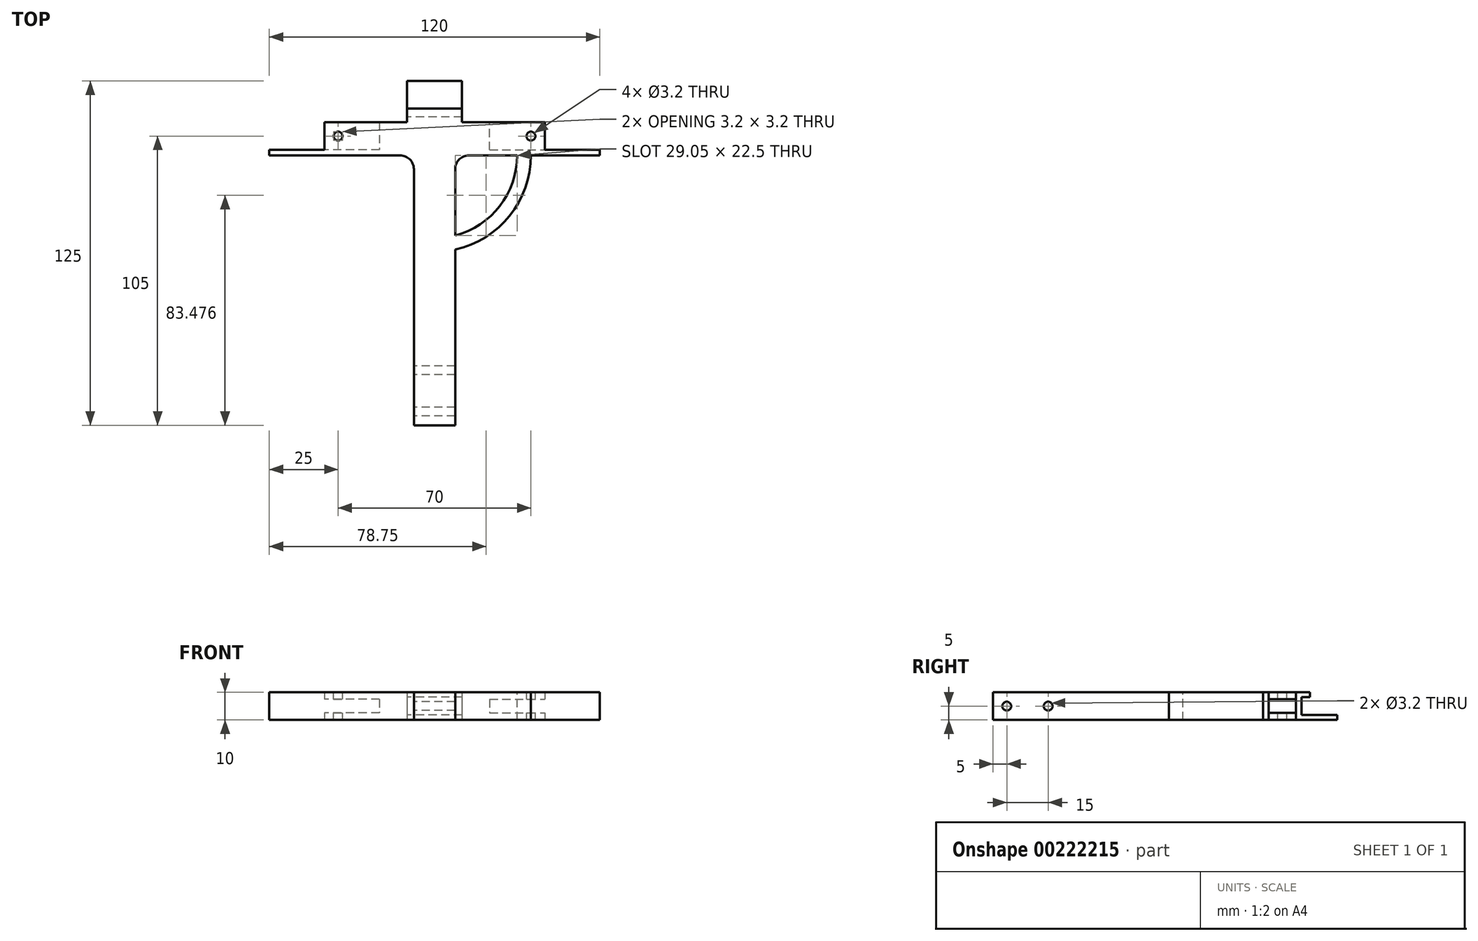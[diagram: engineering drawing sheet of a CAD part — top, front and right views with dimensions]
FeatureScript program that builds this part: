
annotation { "Feature Type Name" : "Feature", "Feature Type Description" : "" }
export const myFeature = defineFeature(function(context is Context, id is Id, definition is map)
    precondition{}
    {
        {
            var Q0;
            Q0=qCreatedBy(makeId("Top.planeOp"),FACE);
            var sketch = newSketch(context, id + "F0", { "sketchPlane" : qUnion([Q0])});
            skLineSegment(sketch, "E0.bottom", {"start": v(-7.5, 50) * mm, "end": v(7.5, 50) * mm});
            skLineSegment(sketch, "E0.top", {"start": v(-7.5, -50) * mm, "end": v(7.5, -50) * mm});
            skLineSegment(sketch, "E0.left", {"start": v(-7.5, 50) * mm, "end": v(-7.5, -50) * mm});
            skLineSegment(sketch, "E0.right", {"start": v(7.5, 50) * mm, "end": v(7.5, -50) * mm});
            skPoint(sketch, "E1", {"position": v(0, 50) * mm});
            skPoint(sketch, "E2", {"position": v(-7.5, 0) * mm});
            skSolve(sketch);
        }
        {
            var Q0;
            Q0=makeQuery(id+"F0.imprint","IMPRINT",FACE,{"disambiguationData":[TD([[makeQuery(id+"F0.imprint","IMPRINT",EDGE,{"derivedFrom":sQuery(id+"F0.wireOp",EDGE,"E0.bottom")}),-1.0]])]});
            extrude(context, id + "F1", {"entities" : qUnion([Q0]), "endBound" : BoundingType.SYMMETRIC, "depth" : 10 * mm});
        }
        {
            var Q0;
            Q0=makeQuery(id+"F1.opExtrude","SWEPT_FACE",FACE,{"disambiguationData":[OSD([sQuery(id+"F0.wireOp",EDGE,"E0.bottom")])]});
            var sketch = newSketch(context, id + "F2", { "sketchPlane" : qUnion([Q0])});
            skLineSegment(sketch, "E3.bottom", {"start": v(-40, 5) * mm, "end": v(40, 5) * mm});
            skLineSegment(sketch, "E3.top", {"start": v(-40, -5) * mm, "end": v(40, -5) * mm});
            skLineSegment(sketch, "E3.left", {"start": v(-40, 5) * mm, "end": v(-40, -5) * mm});
            skLineSegment(sketch, "E3.right", {"start": v(40, 5) * mm, "end": v(40, -5) * mm});
            skPoint(sketch, "E4", {"position": v(-40, 0) * mm});
            skPoint(sketch, "E5", {"position": v(0, 5) * mm});
            skSolve(sketch);
        }
        {
            var Q0;
            Q0 = qSketchRegion(id + "F2", true);
            extrude(context, id + "F3", {"entities" : qUnion([Q0]), "operationType" : NewBodyOperationType.ADD, "depth" : 10 * mm});
        }
        {
            var Q0;
            Q0=makeQuery(id+"F3.opExtrude","SWEPT_FACE",FACE,{"disambiguationData":[OSD([sQuery(id+"F2.wireOp",EDGE,"E3.right")])]});
            var sketch = newSketch(context, id + "F4", { "sketchPlane" : qUnion([Q0])});
            skLineSegment(sketch, "E6.bottom", {"start": v(-60, -2.5) * mm, "end": v(-50, -2.5) * mm});
            skLineSegment(sketch, "E6.top", {"start": v(-60, 2.5) * mm, "end": v(-50, 2.5) * mm});
            skLineSegment(sketch, "E6.left", {"start": v(-60, -2.5) * mm, "end": v(-60, 2.5) * mm});
            skLineSegment(sketch, "E6.right", {"start": v(-50, -2.5) * mm, "end": v(-50, 2.5) * mm});
            skPoint(sketch, "E7", {"position": v(-60, 0) * mm});
            skSolve(sketch);
        }
        {
            var Q0;
            Q0=makeQuery(id+"F4.imprint","IMPRINT",FACE,{"disambiguationData":[TD([[makeQuery(id+"F4.imprint","IMPRINT",EDGE,{"derivedFrom":sQuery(id+"F4.wireOp",EDGE,"E6.bottom")}),1.0]])]});
            extrude(context, id + "F5", {"entities" : qUnion([Q0]), "operationType" : NewBodyOperationType.REMOVE, "oppositeDirection" : true, "depth" : 20 * mm});
        }
        {
            var Q0;
            Q0=makeQuery(id+"F3.opExtrude","SWEPT_FACE",FACE,{"disambiguationData":[OSD([sQuery(id+"F2.wireOp",EDGE,"E3.left")])]});
            var sketch = newSketch(context, id + "F6", { "sketchPlane" : qUnion([Q0])});
            skLineSegment(sketch, "E8.bottom", {"start": v(50, 2.5) * mm, "end": v(60, 2.5) * mm});
            skLineSegment(sketch, "E8.top", {"start": v(50, -2.5) * mm, "end": v(60, -2.5) * mm});
            skLineSegment(sketch, "E8.left", {"start": v(50, 2.5) * mm, "end": v(50, -2.5) * mm});
            skLineSegment(sketch, "E8.right", {"start": v(60, 2.5) * mm, "end": v(60, -2.5) * mm});
            skPoint(sketch, "E9", {"position": v(50, 0) * mm});
            skSolve(sketch);
        }
        {
            var Q0;
            Q0=makeQuery(id+"F6.imprint","IMPRINT",FACE,{"disambiguationData":[TD([[makeQuery(id+"F6.imprint","IMPRINT",EDGE,{"derivedFrom":sQuery(id+"F6.wireOp",EDGE,"E8.bottom")}),-1.0]])]});
            extrude(context, id + "F7", {"entities" : qUnion([Q0]), "operationType" : NewBodyOperationType.REMOVE, "oppositeDirection" : true, "depth" : 20 * mm});
        }
        {
            var Q0;
            Q0=makeQuery(id+"F3.boolean.opBoolean","MERGE",FACE,{"derivedFrom":[makeQuery(id+"F1.opExtrude","CAP_FACE",FACE,{"disambiguationData":[OSD([sQuery(id+"F0.wireOp",EDGE,"E0.bottom"),sQuery(id+"F0.wireOp",EDGE,"E0.top"),sQuery(id+"F0.wireOp",EDGE,"E0.left"),sQuery(id+"F0.wireOp",EDGE,"E0.right")])],"isStart":false}),makeQuery(id+"F3.opExtrude","SWEPT_FACE",FACE,{"disambiguationData":[OSD([sQuery(id+"F2.wireOp",EDGE,"E3.bottom")])]})]});
            var sketch = newSketch(context, id + "F8", { "sketchPlane" : qUnion([Q0])});
            skCircle(sketch, "E10", {"center": v(-35, 55) * mm, "radius": 1.6 * mm});
            skCircle(sketch, "E11", {"center": v(35, 55) * mm, "radius": 1.6 * mm});
            skLineSegment(sketch, "E12", {"start": v(-35, 55) * mm, "end": v(35, 55) * mm, "construction": true});
            skPoint(sketch, "E13", {"position": v(0, 55) * mm});
            skPoint(sketch, "E14", {"position": v(-40, 55) * mm});
            skSolve(sketch);
        }
        {
            var Q0;
            Q0=makeQuery(id+"F8.imprint","IMPRINT",FACE,{"disambiguationData":[TD([[makeQuery(id+"F8.imprint","IMPRINT",EDGE,{"derivedFrom":sQuery(id+"F8.wireOp",EDGE,"E10")}),1.0]])]});
            var Q1;
            Q1=makeQuery(id+"F8.imprint","IMPRINT",FACE,{"disambiguationData":[TD([[makeQuery(id+"F8.imprint","IMPRINT",EDGE,{"derivedFrom":sQuery(id+"F8.wireOp",EDGE,"E11")}),1.0]])]});
            var Q2;
            Q2=sQuery(id+"F8.wireOp",EDGE,"E10");
            var Q3;
            Q3=makeQuery(id+"F3.boolean.opBoolean","MERGE",FACE,{"derivedFrom":[makeQuery(id+"F1.opExtrude","CAP_FACE",FACE,{"disambiguationData":[OSD([sQuery(id+"F0.wireOp",EDGE,"E0.bottom"),sQuery(id+"F0.wireOp",EDGE,"E0.top"),sQuery(id+"F0.wireOp",EDGE,"E0.left"),sQuery(id+"F0.wireOp",EDGE,"E0.right")])],"isStart":true}),makeQuery(id+"F3.opExtrude","SWEPT_FACE",FACE,{"disambiguationData":[OSD([sQuery(id+"F2.wireOp",EDGE,"E3.top")])]})]});
            extrude(context, id + "F9", {"entities" : qUnion([Q0, Q1]), "operationType" : NewBodyOperationType.REMOVE, "surfaceEntities" : qUnion([Q2]), "endBound" : BoundingType.UP_TO_SURFACE, "oppositeDirection" : true, "endBoundEntityFace" : qUnion([Q3]), "depth" : 25 * mm});
        }
        {
            var Q0;
            {var subQ0=sQuery(id+"F0.wireOp",EDGE,"E0.left");var subQ4=sQuery(id+"F2.wireOp",EDGE,"E3.bottom");var subQ5=sQuery(id+"F2.wireOp",EDGE,"E3.right");var subQ6=sQuery(id+"F2.wireOp",EDGE,"E3.top");Q0=makeQuery(id+"F3.boolean.opBoolean","SPLIT",FACE,{"disambiguationData":[TD([makeQuery(id+"F1.opExtrude","SWEPT_FACE",FACE,{"disambiguationData":[OSD([subQ0])]})])],"derivedFrom":makeQuery(id+"F3.opExtrude","CAP_FACE",FACE,{"disambiguationData":[OSD([subQ4,subQ6,sQuery(id+"F2.wireOp",EDGE,"E3.left"),subQ5])],"isStart":true})});}
            var sketch = newSketch(context, id + "F10", { "sketchPlane" : qUnion([Q0])});
            skPoint(sketch, "E15.oppositeSnap0", {"position": v(-23.75, -5) * mm});
            skLineSegment(sketch, "E15.bottom", {"start": v(-60, 5) * mm, "end": v(60, 5) * mm});
            skLineSegment(sketch, "E15.top", {"start": v(-60, -5) * mm, "end": v(60, -5) * mm});
            skLineSegment(sketch, "E15.left", {"start": v(-60, 5) * mm, "end": v(-60, -5) * mm});
            skLineSegment(sketch, "E15.right", {"start": v(60, 5) * mm, "end": v(60, -5) * mm});
            skPoint(sketch, "E16", {"position": v(0, 5) * mm});
            skSolve(sketch);
        }
        {
            var Q0;
            {var subQ2=sQuery(id+"F10.wireOp",EDGE,"E15.right");Q0=makeQuery(id+"F10.imprint","IMPRINT",FACE,{"disambiguationData":[TD([[makeQuery(id+"F10.imprint","IMPRINT",EDGE,{"derivedFrom":subQ2}),-1.0]])]});}
            var Q1;
            Q1 = qSketchRegion(id + "F10", true);
            extrude(context, id + "F11", {"entities" : qUnion([Q0, Q1]), "operationType" : NewBodyOperationType.ADD, "depth" : 2 * mm});
        }
        {
            var Q0;
            Q0=makeQuery(id+"F11.boolean.opBoolean","INTERSECT",EDGE,{"derivedFrom":[makeQuery(id+"F1.opExtrude","SWEPT_FACE",FACE,{"disambiguationData":[OSD([sQuery(id+"F0.wireOp",EDGE,"E0.left")])]}),makeQuery(id+"F11.opExtrude","CAP_FACE",FACE,{"disambiguationData":[OSD([sQuery(id+"F10.wireOp",EDGE,"E15.bottom"),sQuery(id+"F10.wireOp",EDGE,"E15.top"),sQuery(id+"F10.wireOp",EDGE,"E15.left"),sQuery(id+"F10.wireOp",EDGE,"E15.right")])],"isStart":false})]});
            var Q1;
            Q1=makeQuery(id+"F11.boolean.opBoolean","INTERSECT",EDGE,{"derivedFrom":[makeQuery(id+"F1.opExtrude","SWEPT_FACE",FACE,{"disambiguationData":[OSD([sQuery(id+"F0.wireOp",EDGE,"E0.right")])]}),makeQuery(id+"F11.opExtrude","CAP_FACE",FACE,{"disambiguationData":[OSD([sQuery(id+"F10.wireOp",EDGE,"E15.bottom"),sQuery(id+"F10.wireOp",EDGE,"E15.top"),sQuery(id+"F10.wireOp",EDGE,"E15.left"),sQuery(id+"F10.wireOp",EDGE,"E15.right")])],"isStart":false})]});
            fillet(context, id + "F12", {"entities" : qUnion([Q0, Q1]), "radius" : 5 * mm, "tangentPropagation" : true, "allowEdgeOverflow" : false});
        }
        {
            var Q0;
            Q0=makeQuery(id+"F1.opExtrude","SWEPT_FACE",FACE,{"disambiguationData":[OSD([sQuery(id+"F0.wireOp",EDGE,"E0.left")])]});
            var sketch = newSketch(context, id + "F13", { "sketchPlane" : qUnion([Q0])});
            skCircle(sketch, "E17", {"center": v(45, 0) * mm, "radius": 1.6 * mm});
            skCircle(sketch, "E18", {"center": v(30, 0) * mm, "radius": 1.6 * mm});
            skSolve(sketch);
        }
        {
            var Q0;
            Q0=makeQuery(id+"F13.imprint","IMPRINT",FACE,{"disambiguationData":[TD([[makeQuery(id+"F13.imprint","IMPRINT",EDGE,{"derivedFrom":sQuery(id+"F13.wireOp",EDGE,"E18")}),1.0]])]});
            var Q1;
            Q1=makeQuery(id+"F13.imprint","IMPRINT",FACE,{"disambiguationData":[TD([[makeQuery(id+"F13.imprint","IMPRINT",EDGE,{"derivedFrom":sQuery(id+"F13.wireOp",EDGE,"E17")}),1.0]])]});
            extrude(context, id + "F14", {"entities" : qUnion([Q0, Q1]), "operationType" : NewBodyOperationType.REMOVE, "endBound" : BoundingType.UP_TO_NEXT, "oppositeDirection" : true, "depth" : 25 * mm});
        }
        {
            var Q0;
            Q0=makeQuery(id+"F3.opExtrude","CAP_FACE",FACE,{"disambiguationData":[OSD([sQuery(id+"F2.wireOp",EDGE,"E3.bottom"),sQuery(id+"F2.wireOp",EDGE,"E3.top"),sQuery(id+"F2.wireOp",EDGE,"E3.left"),sQuery(id+"F2.wireOp",EDGE,"E3.right")])],"isStart":false});
            var sketch = newSketch(context, id + "F15", { "sketchPlane" : qUnion([Q0])});
            skLineSegment(sketch, "E19.bottom", {"start": v(-10, 5) * mm, "end": v(10, 5) * mm});
            skLineSegment(sketch, "E19.top", {"start": v(-10, -5) * mm, "end": v(10, -5) * mm});
            skLineSegment(sketch, "E19.left", {"start": v(-10, 5) * mm, "end": v(-10, -5) * mm});
            skLineSegment(sketch, "E19.right", {"start": v(10, 5) * mm, "end": v(10, -5) * mm});
            skPoint(sketch, "E20", {"position": v(0, 5) * mm});
            skSolve(sketch);
        }
        {
            var Q0;
            Q0=makeQuery(id+"F15.imprint","IMPRINT",FACE,{"disambiguationData":[TD([[makeQuery(id+"F15.imprint","IMPRINT",EDGE,{"derivedFrom":sQuery(id+"F15.wireOp",EDGE,"E19.bottom")}),-1.0]])]});
            extrude(context, id + "F16", {"entities" : qUnion([Q0]), "operationType" : NewBodyOperationType.ADD, "depth" : 5 * mm});
        }
        {
            var Q0;
            Q0=makeQuery(id+"F16.opExtrude","CAP_FACE",FACE,{"disambiguationData":[OSD([sQuery(id+"F15.wireOp",EDGE,"E19.bottom"),sQuery(id+"F15.wireOp",EDGE,"E19.top"),sQuery(id+"F15.wireOp",EDGE,"E19.left"),sQuery(id+"F15.wireOp",EDGE,"E19.right")])],"isStart":false});
            var sketch = newSketch(context, id + "F17", { "sketchPlane" : qUnion([Q0])});
            skLineSegment(sketch, "E21.bottom", {"start": v(-10, 3.25) * mm, "end": v(10, 3.25) * mm});
            skLineSegment(sketch, "E21.top", {"start": v(-10, -3.25) * mm, "end": v(10, -3.25) * mm});
            skLineSegment(sketch, "E21.left", {"start": v(-10, 3.25) * mm, "end": v(-10, -3.25) * mm});
            skLineSegment(sketch, "E21.right", {"start": v(10, 3.25) * mm, "end": v(10, -3.25) * mm});
            skPoint(sketch, "E22", {"position": v(-10, 0) * mm});
            skSolve(sketch);
        }
        {
            var Q0;
            Q0=makeQuery(id+"F17.imprint","IMPRINT",FACE,{"disambiguationData":[TD([[makeQuery(id+"F17.imprint","IMPRINT",EDGE,{"derivedFrom":sQuery(id+"F17.wireOp",EDGE,"E21.bottom")}),-1.0]])]});
            extrude(context, id + "F18", {"entities" : qUnion([Q0]), "operationType" : NewBodyOperationType.REMOVE, "oppositeDirection" : true, "depth" : 3 * mm});
        }
        {
            var Q0;
            {var subQ0=sQuery(id+"F15.wireOp",EDGE,"E19.top");var subQ1=sQuery(id+"F15.wireOp",EDGE,"E19.left");var subQ2=sQuery(id+"F15.wireOp",EDGE,"E19.right");Q0=makeQuery(id+"F18.boolean.opBoolean","SPLIT",FACE,{"disambiguationData":[TD([makeQuery(id+"F3.opExtrude","SWEPT_FACE",FACE,{"disambiguationData":[OSD([sQuery(id+"F2.wireOp",EDGE,"E3.top")])]})])],"derivedFrom":makeQuery(id+"F16.opExtrude","CAP_FACE",FACE,{"disambiguationData":[OSD([sQuery(id+"F15.wireOp",EDGE,"E19.bottom"),subQ0,subQ1,subQ2])],"isStart":false})});}
            extrude(context, id + "F19", {"entities" : qUnion([Q0]), "operationType" : NewBodyOperationType.ADD, "depth" : 10 * mm});
        }
        {
            var Q0;
            Q0=makeQuery(id+"F16.boolean.opBoolean","MERGE",FACE,{"derivedFrom":[makeQuery(id+"F11.boolean.opBoolean","MERGE",FACE,{"derivedFrom":[makeQuery(id+"F3.boolean.opBoolean","MERGE",FACE,{"derivedFrom":[makeQuery(id+"F1.opExtrude","CAP_FACE",FACE,{"disambiguationData":[OSD([sQuery(id+"F0.wireOp",EDGE,"E0.bottom"),sQuery(id+"F0.wireOp",EDGE,"E0.top"),sQuery(id+"F0.wireOp",EDGE,"E0.left"),sQuery(id+"F0.wireOp",EDGE,"E0.right")])],"isStart":false}),makeQuery(id+"F3.opExtrude","SWEPT_FACE",FACE,{"disambiguationData":[OSD([sQuery(id+"F2.wireOp",EDGE,"E3.bottom")])]})]}),makeQuery(id+"F11.opExtrude","SWEPT_FACE",FACE,{"disambiguationData":[OSD([sQuery(id+"F10.wireOp",EDGE,"E15.bottom")])]})]}),makeQuery(id+"F16.opExtrude","SWEPT_FACE",FACE,{"disambiguationData":[OSD([sQuery(id+"F15.wireOp",EDGE,"E19.bottom")])]})]});
            var sketch = newSketch(context, id + "F20", { "sketchPlane" : qUnion([Q0])});
            skArc(sketch, "E23", {"start": v(30, 48) * mm, "mid": v(21.21, 26.79) * mm, "end": v(0, 18) * mm});
            skArc(sketch, "E24", {"start": v(35, 48) * mm, "mid": v(24.75, 23.25) * mm, "end": v(0, 13) * mm});
            skLineSegment(sketch, "E25", {"start": v(0, 18) * mm, "end": v(0, 13) * mm});
            skLineSegment(sketch, "E26", {"start": v(30, 48) * mm, "end": v(35, 48) * mm});
            skSolve(sketch);
        }
        {
            var Q0;
            {var subQ0=sQuery(id+"F20.wireOp",EDGE,"E26");Q0=makeQuery(id+"F20.imprint","IMPRINT",FACE,{"disambiguationData":[TD([[makeQuery(id+"F20.imprint","IMPRINT",EDGE,{"derivedFrom":subQ0}),-1.0]])]});}
            var Q1;
            {var subQ0=sQuery(id+"F15.wireOp",EDGE,"E19.top");Q1=makeQuery(id+"F19.boolean.opBoolean","MERGE",FACE,{"derivedFrom":[makeQuery(id+"F16.boolean.opBoolean","MERGE",FACE,{"derivedFrom":[makeQuery(id+"F11.boolean.opBoolean","MERGE",FACE,{"derivedFrom":[makeQuery(id+"F3.boolean.opBoolean","MERGE",FACE,{"derivedFrom":[makeQuery(id+"F1.opExtrude","CAP_FACE",FACE,{"disambiguationData":[OSD([sQuery(id+"F0.wireOp",EDGE,"E0.bottom"),sQuery(id+"F0.wireOp",EDGE,"E0.top"),sQuery(id+"F0.wireOp",EDGE,"E0.left"),sQuery(id+"F0.wireOp",EDGE,"E0.right")])],"isStart":true}),makeQuery(id+"F3.opExtrude","SWEPT_FACE",FACE,{"disambiguationData":[OSD([sQuery(id+"F2.wireOp",EDGE,"E3.top")])]})]}),makeQuery(id+"F11.opExtrude","SWEPT_FACE",FACE,{"disambiguationData":[OSD([sQuery(id+"F10.wireOp",EDGE,"E15.top")])]})]}),makeQuery(id+"F16.opExtrude","SWEPT_FACE",FACE,{"disambiguationData":[OSD([subQ0])]})]}),makeQuery(id+"F19.opExtrude","SWEPT_FACE",FACE,{"disambiguationData":[OSD([subQ0])]})]});}
            extrude(context, id + "F21", {"entities" : qUnion([Q0]), "operationType" : NewBodyOperationType.ADD, "endBound" : BoundingType.UP_TO_SURFACE, "oppositeDirection" : true, "endBoundEntityFace" : qUnion([Q1]), "depth" : 25 * mm});
        }
    });
